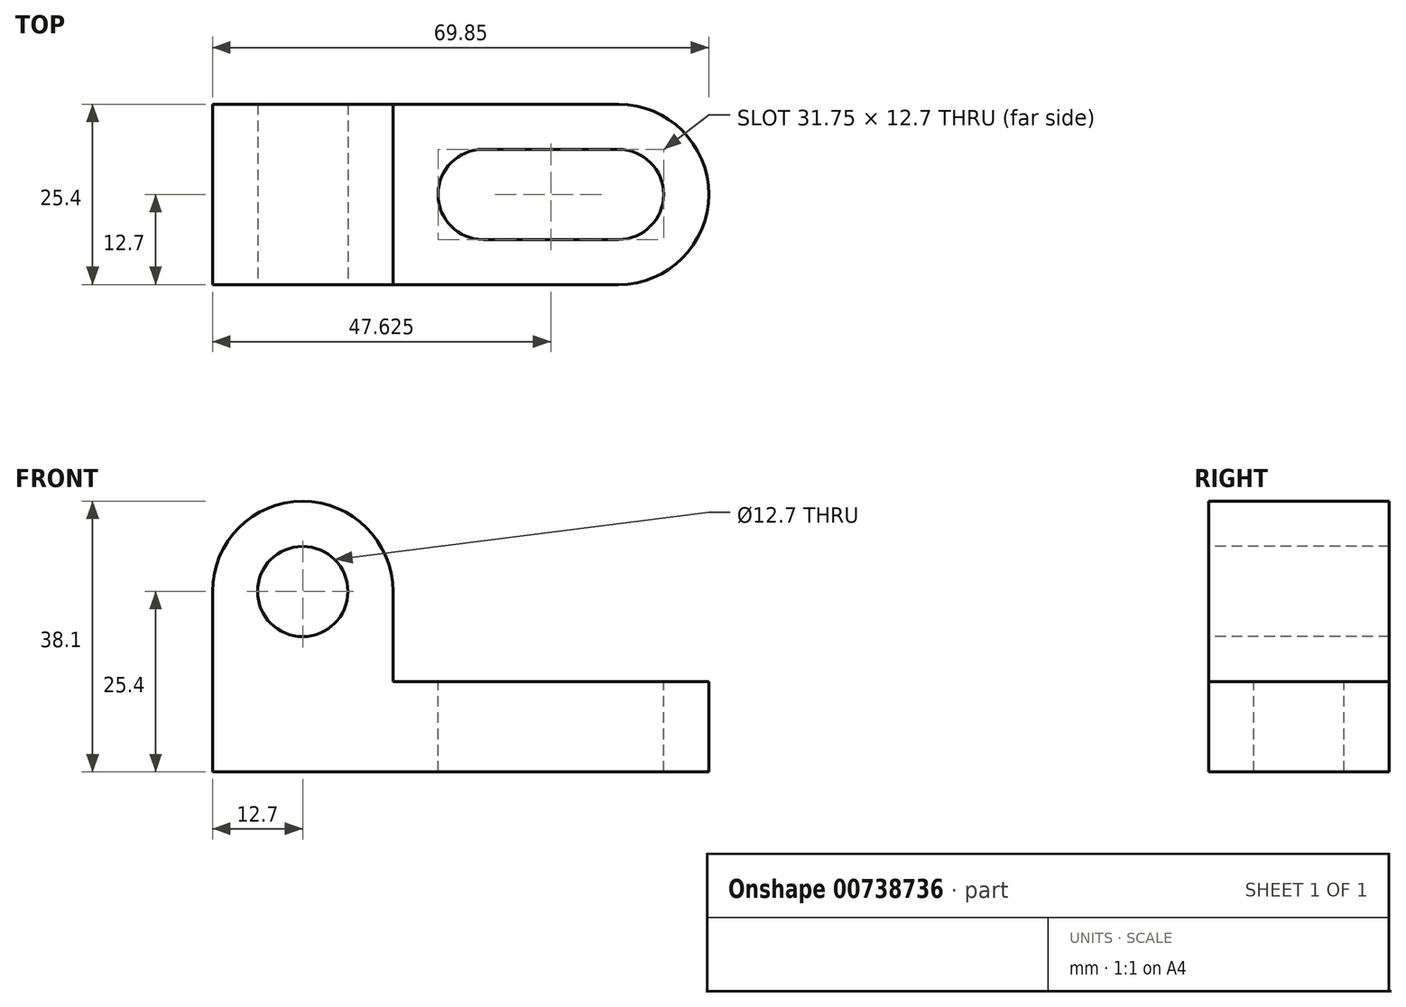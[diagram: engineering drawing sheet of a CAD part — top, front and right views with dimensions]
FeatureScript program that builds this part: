
annotation { "Feature Type Name" : "Feature", "Feature Type Description" : "" }
export const myFeature = defineFeature(function(context is Context, id is Id, definition is map)
    precondition{}
    {
        {
            var Q0;
            Q0=qCreatedBy(makeId("Front.planeOp"),FACE);
            var sketch = newSketch(context, id + "F0", { "sketchPlane" : qUnion([Q0])});
            skLineSegment(sketch, "E0", {"start": v(0, 0) * mm, "end": v(0, 38.1) * mm});
            skLineSegment(sketch, "E1", {"start": v(0, 38.1) * mm, "end": v(25.4, 38.1) * mm});
            skLineSegment(sketch, "E2", {"start": v(25.4, 38.1) * mm, "end": v(25.4, 12.7) * mm});
            skLineSegment(sketch, "E3", {"start": v(25.4, 12.7) * mm, "end": v(69.85, 12.7) * mm});
            skLineSegment(sketch, "E4", {"start": v(69.85, 12.7) * mm, "end": v(69.85, 0) * mm});
            skLineSegment(sketch, "E5", {"start": v(69.85, 0) * mm, "end": v(0, 0) * mm});
            skSolve(sketch);
        }
        {
            var Q0;
            Q0 = qSketchRegion(id + "F0", true);
            extrude(context, id + "F1", {"entities" : qUnion([Q0]), "depth" : 25.4 * mm, "offsetDistance" : 25.4 * mm});
        }
        {
            var Q0;
            Q0=makeQuery(id+"F1.opExtrude","CAP_FACE",FACE,{"disambiguationData":[OSD([sQuery(id+"F0.wireOp",EDGE,"E0"),sQuery(id+"F0.wireOp",EDGE,"E1"),sQuery(id+"F0.wireOp",EDGE,"E2"),sQuery(id+"F0.wireOp",EDGE,"E3"),sQuery(id+"F0.wireOp",EDGE,"E4"),sQuery(id+"F0.wireOp",EDGE,"E5")])],"isStart":false});
            var sketch = newSketch(context, id + "F2", { "sketchPlane" : qUnion([Q0])});
            skLineSegment(sketch, "E6", {"start": v(0, 25.4) * mm, "end": v(25.4, 25.4) * mm});
            skCircle(sketch, "E7", {"center": v(12.7, 25.4) * mm, "radius": 6.35 * mm});
            skArc(sketch, "E8", {"start": v(25.4, 25.4) * mm, "mid": v(12.7, 38.1) * mm, "end": v(0, 25.4) * mm});
            skSolve(sketch);
        }
        {
            var Q0;
            {var subQ0=sQuery(id+"F2.wireOp",EDGE,"E7");var subQ1=sQuery(id+"F2.wireOp",EDGE,"E6");var subQ2=makeQuery(id+"F2.imprint","INTERSECT",VERTEX,{"disambiguationData":[OD(0.0)],"derivedFrom":[subQ1,subQ0]});Q0=makeQuery(id+"F2.imprint","IMPRINT",FACE,{"disambiguationData":[TD([[makeQuery(id+"F2.imprint","IMPRINT",EDGE,{"disambiguationData":[TD([[subQ2,-1.0]])],"derivedFrom":subQ1}),1.0]])]});}
            var Q1;
            {var subQ0=sQuery(id+"F2.wireOp",EDGE,"E7");var subQ1=sQuery(id+"F2.wireOp",EDGE,"E6");var subQ2=makeQuery(id+"F2.imprint","INTERSECT",VERTEX,{"disambiguationData":[OD(0.0)],"derivedFrom":[subQ1,subQ0]});Q1=makeQuery(id+"F2.imprint","IMPRINT",FACE,{"disambiguationData":[TD([[makeQuery(id+"F2.imprint","IMPRINT",EDGE,{"disambiguationData":[TD([[subQ2,-1.0]])],"derivedFrom":subQ1}),-1.0]])]});}
            var Q2;
            {var subQ1=makeQuery(id+"F1.opExtrude","CAP_EDGE",EDGE,{"disambiguationData":[OSD([sQuery(id+"F0.wireOp",EDGE,"E0")])],"isStart":false});var subQ3=makeQuery(id+"F1.opExtrude","CAP_EDGE",EDGE,{"disambiguationData":[OSD([sQuery(id+"F0.wireOp",EDGE,"E1")])],"isStart":false});var subQ5=makeQuery(id+"F2.imprint","INTERSECT",VERTEX,{"derivedFrom":[subQ1,subQ3]});Q2=makeQuery(id+"F2.imprint","IMPRINT",FACE,{"disambiguationData":[TD([[makeQuery(id+"F2.imprint","IMPRINT",EDGE,{"disambiguationData":[TD([[subQ5,-1.0]])],"derivedFrom":subQ3}),-1.0]])]});}
            var Q3;
            {var subQ1=makeQuery(id+"F1.opExtrude","CAP_EDGE",EDGE,{"disambiguationData":[OSD([sQuery(id+"F0.wireOp",EDGE,"E2")])],"isStart":false});var subQ3=makeQuery(id+"F1.opExtrude","CAP_EDGE",EDGE,{"disambiguationData":[OSD([sQuery(id+"F0.wireOp",EDGE,"E1")])],"isStart":false});var subQ5=makeQuery(id+"F2.imprint","INTERSECT",VERTEX,{"derivedFrom":[subQ3,subQ1]});Q3=makeQuery(id+"F2.imprint","IMPRINT",FACE,{"disambiguationData":[TD([[makeQuery(id+"F2.imprint","IMPRINT",EDGE,{"disambiguationData":[TD([[subQ5,1.0]])],"derivedFrom":subQ3}),-1.0]])]});}
            extrude(context, id + "F3", {"entities" : qUnion([Q0, Q1, Q2, Q3]), "operationType" : NewBodyOperationType.REMOVE, "endBound" : BoundingType.THROUGH_ALL, "oppositeDirection" : true, "depth" : 25.4 * mm, "offsetDistance" : 25.4 * mm});
        }
        {
            var Q0;
            Q0=makeQuery(id+"F1.opExtrude","SWEPT_FACE",FACE,{"disambiguationData":[OSD([sQuery(id+"F0.wireOp",EDGE,"E3")])]});
            var sketch = newSketch(context, id + "F4", { "sketchPlane" : qUnion([Q0])});
            skLineSegment(sketch, "E9", {"start": v(38.1, 0) * mm, "end": v(38.1, -25.4) * mm});
            skLineSegment(sketch, "E10", {"start": v(57.15, 0) * mm, "end": v(57.15, -25.4) * mm});
            skCircle(sketch, "E11", {"center": v(38.1, -12.7) * mm, "radius": 6.35 * mm});
            skCircle(sketch, "E12", {"center": v(57.15, -12.7) * mm, "radius": 6.35 * mm});
            skLineSegment(sketch, "E13", {"start": v(38.1, -6.35) * mm, "end": v(57.15, -6.35) * mm});
            skLineSegment(sketch, "E14", {"start": v(38.1, -19.05) * mm, "end": v(57.15, -19.05) * mm});
            skArc(sketch, "E15", {"start": v(57.15, -25.4) * mm, "mid": v(69.85, -12.7) * mm, "end": v(57.15, 0) * mm});
            skSolve(sketch);
        }
        {
            var Q0;
            {var subQ0=sQuery(id+"F4.wireOp",EDGE,"E11");var subQ1=sQuery(id+"F4.wireOp",EDGE,"E9");var subQ2=makeQuery(id+"F4.imprint","INTERSECT",VERTEX,{"derivedFrom":[subQ1,subQ0,sQuery(id+"F4.wireOp",EDGE,"E13")]});Q0=makeQuery(id+"F4.imprint","IMPRINT",FACE,{"disambiguationData":[TD([[makeQuery(id+"F4.imprint","IMPRINT",EDGE,{"disambiguationData":[TD([[subQ2,-1.0]])],"derivedFrom":subQ1}),-1.0]])]});}
            var Q1;
            {var subQ0=sQuery(id+"F4.wireOp",EDGE,"E11");var subQ1=sQuery(id+"F4.wireOp",EDGE,"E9");var subQ2=makeQuery(id+"F4.imprint","INTERSECT",VERTEX,{"derivedFrom":[subQ1,subQ0,sQuery(id+"F4.wireOp",EDGE,"E13")]});Q1=makeQuery(id+"F4.imprint","IMPRINT",FACE,{"disambiguationData":[TD([[makeQuery(id+"F4.imprint","IMPRINT",EDGE,{"disambiguationData":[TD([[subQ2,-1.0]])],"derivedFrom":subQ1}),1.0]])]});}
            var Q2;
            {var subQ0=sQuery(id+"F4.wireOp",EDGE,"E13");Q2=makeQuery(id+"F4.imprint","IMPRINT",FACE,{"disambiguationData":[TD([[makeQuery(id+"F4.imprint","IMPRINT",EDGE,{"derivedFrom":subQ0}),-1.0]])]});}
            var Q3;
            {var subQ0=sQuery(id+"F4.wireOp",EDGE,"E12");var subQ1=sQuery(id+"F4.wireOp",EDGE,"E10");var subQ2=makeQuery(id+"F4.imprint","INTERSECT",VERTEX,{"derivedFrom":[subQ1,subQ0,sQuery(id+"F4.wireOp",EDGE,"E13")]});Q3=makeQuery(id+"F4.imprint","IMPRINT",FACE,{"disambiguationData":[TD([[makeQuery(id+"F4.imprint","IMPRINT",EDGE,{"disambiguationData":[TD([[subQ2,-1.0]])],"derivedFrom":subQ1}),1.0]])]});}
            var Q4;
            {var subQ0=sQuery(id+"F4.wireOp",EDGE,"E15");var subQ1=sQuery(id+"F0.wireOp",EDGE,"E3");var subQ2=makeQuery(id+"F1.opExtrude","CAP_EDGE",EDGE,{"disambiguationData":[OSD([subQ1])],"isStart":false});var subQ3=makeQuery(id+"F4.imprint","INTERSECT",VERTEX,{"derivedFrom":[subQ2,sQuery(id+"F4.wireOp",EDGE,"E10"),subQ0]});Q4=makeQuery(id+"F4.imprint","IMPRINT",FACE,{"disambiguationData":[TD([[makeQuery(id+"F4.imprint","IMPRINT",EDGE,{"disambiguationData":[TD([[subQ3,-1.0]])],"derivedFrom":subQ0}),-1.0]])]});}
            var Q5;
            {var subQ0=sQuery(id+"F4.wireOp",EDGE,"E15");var subQ1=sQuery(id+"F0.wireOp",EDGE,"E3");var subQ2=makeQuery(id+"F1.opExtrude","CAP_EDGE",EDGE,{"disambiguationData":[OSD([subQ1])],"isStart":true});var subQ3=makeQuery(id+"F4.imprint","INTERSECT",VERTEX,{"derivedFrom":[subQ2,sQuery(id+"F4.wireOp",EDGE,"E10"),subQ0]});Q5=makeQuery(id+"F4.imprint","IMPRINT",FACE,{"disambiguationData":[TD([[makeQuery(id+"F4.imprint","IMPRINT",EDGE,{"disambiguationData":[TD([[subQ3,1.0]])],"derivedFrom":subQ0}),-1.0]])]});}
            extrude(context, id + "F5", {"entities" : qUnion([Q0, Q1, Q2, Q3, Q4, Q5]), "operationType" : NewBodyOperationType.REMOVE, "oppositeDirection" : true, "depth" : 25.4 * mm, "offsetDistance" : 25.4 * mm});
        }
        {
            var Q0;
            {var subQ0=sQuery(id+"F4.wireOp",EDGE,"E10");Q0=makeQuery(id+"F5.boolean.opBoolean","SPLIT",FACE,{"disambiguationData":[TD([makeQuery(id+"F5.opExtrude","SWEPT_FACE",FACE,{"disambiguationData":[OSD([subQ0])]})])],"derivedFrom":makeQuery(id+"F1.opExtrude","SWEPT_FACE",FACE,{"disambiguationData":[OSD([sQuery(id+"F0.wireOp",EDGE,"E5")])]})});}
            extrude(context, id + "F6", {"entities" : qUnion([Q0]), "operationType" : NewBodyOperationType.REMOVE, "oppositeDirection" : true, "depth" : 25.4 * mm, "offsetDistance" : 25.4 * mm});
        }
    });
